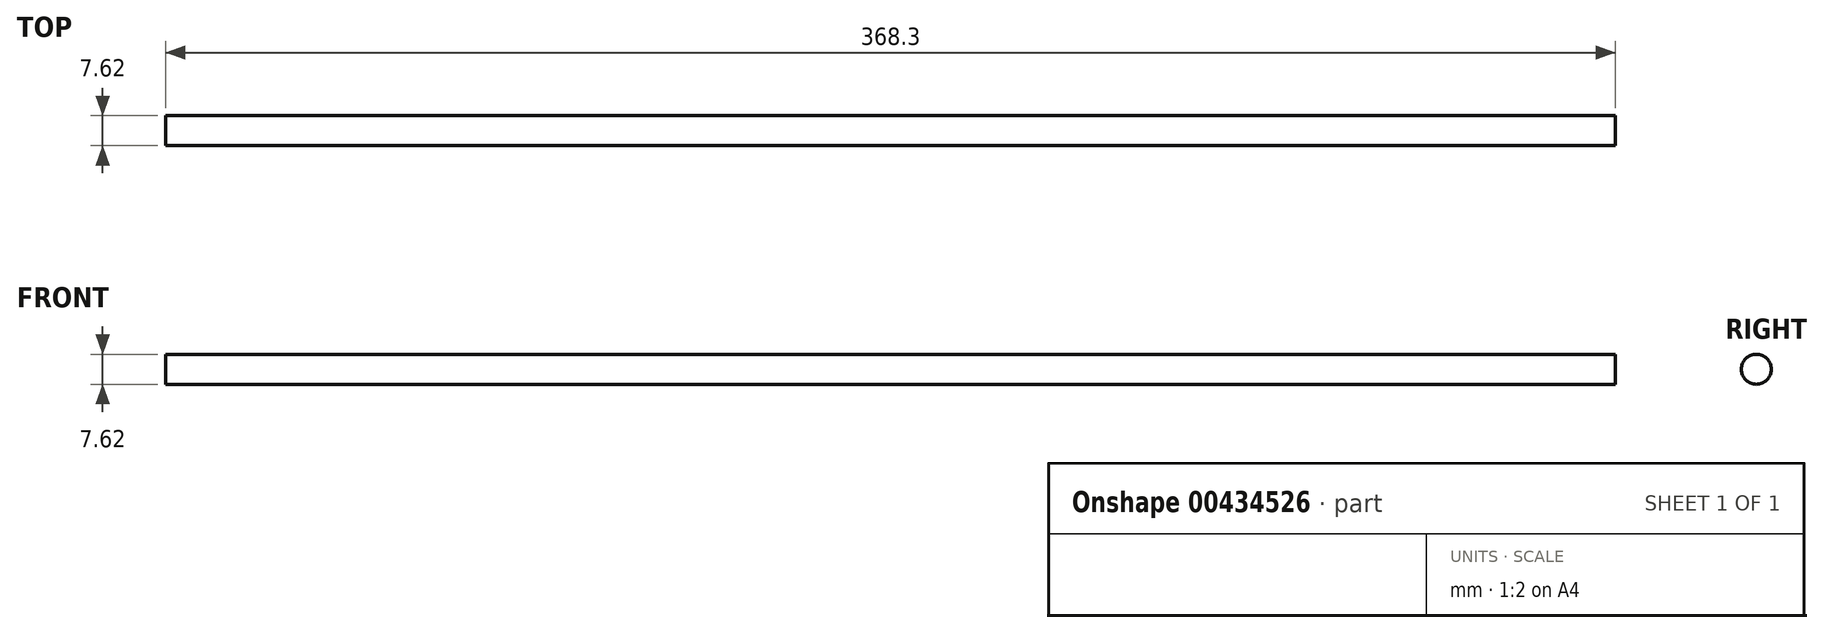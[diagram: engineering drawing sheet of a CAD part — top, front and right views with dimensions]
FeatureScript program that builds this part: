
annotation { "Feature Type Name" : "Feature", "Feature Type Description" : "" }
export const myFeature = defineFeature(function(context is Context, id is Id, definition is map)
    precondition{}
    {
        {
            var Q0;
            Q0=qCreatedBy(makeId("Right.planeOp"),FACE);
            var sketch = newSketch(context, id + "F0", { "sketchPlane" : qUnion([Q0])});
            skCircle(sketch, "E0", {"center": v(0, 0) * mm, "radius": 3.81 * mm});
            skSolve(sketch);
        }
        {
            var Q0;
            Q0 = qSketchRegion(id + "F0", true);
            extrude(context, id + "F1", {"entities" : qUnion([Q0]), "depth" : 368.3 * mm});
        }
    });
